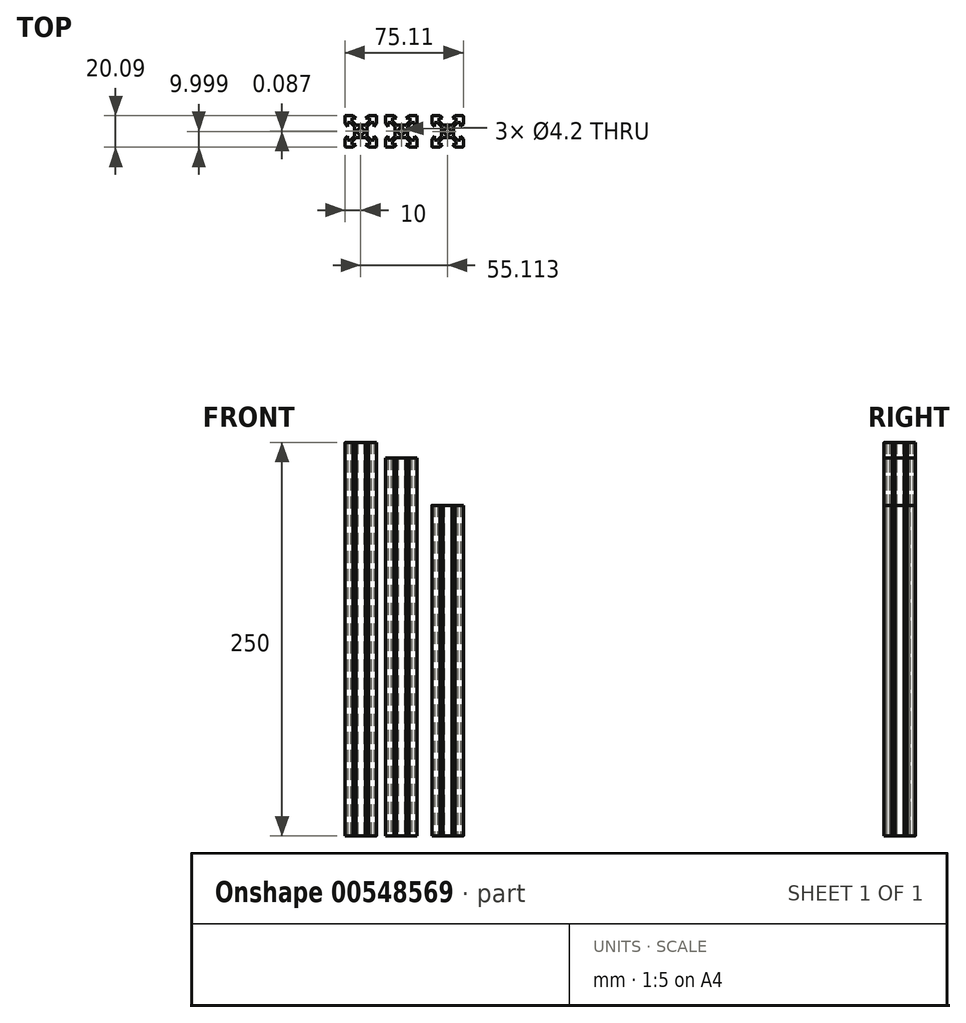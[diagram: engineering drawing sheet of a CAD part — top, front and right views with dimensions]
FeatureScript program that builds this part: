
annotation { "Feature Type Name" : "Feature", "Feature Type Description" : "" }
export const myFeature = defineFeature(function(context is Context, id is Id, definition is map)
    precondition{}
    {
        {
            var Q0;
            Q0=qCreatedBy(makeId("Top.planeOp"),FACE);
            var sketch = newSketch(context, id + "F0", { "sketchPlane" : qUnion([Q0])});
            skPoint(sketch, "E0.middle", {"position": v(0, 0) * mm});
            skLineSegment(sketch, "E1", {"start": v(10, -9.5) * mm, "end": v(10, -4.78) * mm});
            skLineSegment(sketch, "E2", {"start": v(9.5, -10) * mm, "end": v(4.78, -10) * mm});
            skCircle(sketch, "E3", {"center": v(0, 0) * mm, "radius": 2.1 * mm});
            skLineSegment(sketch, "E4", {"start": v(8.32, -3.1) * mm, "end": v(8.32, -5.5) * mm});
            skLineSegment(sketch, "E5", {"start": v(3.1, -8.33) * mm, "end": v(5.5, -8.33) * mm});
            skLineSegment(sketch, "E6", {"start": v(8.32, -3.1) * mm, "end": v(8.32, 0) * mm, "construction": true});
            skLineSegment(sketch, "E7", {"start": v(3.1, -8.33) * mm, "end": v(0, -8.33) * mm, "construction": true});
            skLineSegment(sketch, "E8", {"start": v(5.5, -5.5) * mm, "end": v(5.5, 0) * mm, "construction": true});
            skLineSegment(sketch, "E9", {"start": v(5.5, -5.5) * mm, "end": v(0, -5.5) * mm, "construction": true});
            skLineSegment(sketch, "E10", {"start": v(10, -4.78) * mm, "end": v(10, 0) * mm, "construction": true});
            skLineSegment(sketch, "E11", {"start": v(10, -4.78) * mm, "end": v(8.32, -3.1) * mm});
            skLineSegment(sketch, "E12", {"start": v(4.78, -10) * mm, "end": v(0, -10) * mm, "construction": true});
            skLineSegment(sketch, "E13", {"start": v(4.78, -10) * mm, "end": v(3.1, -8.33) * mm});
            skLineSegment(sketch, "E14", {"start": v(2.98, -3.9) * mm, "end": v(5.5, -6.42) * mm});
            skLineSegment(sketch, "E15", {"start": v(8.32, -5.5) * mm, "end": v(6.42, -5.5) * mm});
            skLineSegment(sketch, "E16", {"start": v(5.5, -8.33) * mm, "end": v(5.5, -6.42) * mm});
            skLineSegment(sketch, "E17.trimOffspring", {"start": v(3.9, -2.98) * mm, "end": v(6.42, -5.5) * mm});
            skLineSegment(sketch, "E18.MirrorCS", {"start": v(8.32, 3.1) * mm, "end": v(8.32, 5.5) * mm});
            skLineSegment(sketch, "E19.MirrorCS", {"start": v(3.1, 8.33) * mm, "end": v(5.5, 8.33) * mm});
            skLineSegment(sketch, "E20.MirrorCS", {"start": v(4.78, 10) * mm, "end": v(3.1, 8.33) * mm});
            skLineSegment(sketch, "E21.MirrorCS", {"start": v(2.98, 3.9) * mm, "end": v(5.5, 6.42) * mm});
            skLineSegment(sketch, "E22.MirrorCS", {"start": v(5.5, 8.33) * mm, "end": v(5.5, 6.42) * mm});
            skLineSegment(sketch, "E23.MirrorCS", {"start": v(10, 9.5) * mm, "end": v(10, 4.78) * mm});
            skLineSegment(sketch, "E24.MirrorCS", {"start": v(8.32, 5.5) * mm, "end": v(6.42, 5.5) * mm});
            skLineSegment(sketch, "E25.MirrorCS", {"start": v(10, 4.78) * mm, "end": v(8.32, 3.1) * mm});
            skLineSegment(sketch, "E26.MirrorCS", {"start": v(9.5, 10) * mm, "end": v(4.78, 10) * mm});
            skLineSegment(sketch, "E27.MirrorCS", {"start": v(3.9, 2.98) * mm, "end": v(6.42, 5.5) * mm});
            skLineSegment(sketch, "E28.MirrorCS", {"start": v(-9.5, 10) * mm, "end": v(-4.78, 10) * mm});
            skLineSegment(sketch, "E29.MirrorCS", {"start": v(-5.5, 8.33) * mm, "end": v(-5.5, 6.42) * mm});
            skLineSegment(sketch, "E30.MirrorCS", {"start": v(-8.32, 5.5) * mm, "end": v(-6.42, 5.5) * mm});
            skLineSegment(sketch, "E31.MirrorCS", {"start": v(-4.78, 10) * mm, "end": v(-3.1, 8.33) * mm});
            skLineSegment(sketch, "E32.MirrorCS", {"start": v(-3.1, 8.33) * mm, "end": v(-5.5, 8.33) * mm});
            skLineSegment(sketch, "E33.MirrorCS", {"start": v(-2.98, 3.9) * mm, "end": v(-5.5, 6.42) * mm});
            skLineSegment(sketch, "E34.MirrorCS", {"start": v(-8.32, 3.1) * mm, "end": v(-8.32, 5.5) * mm});
            skLineSegment(sketch, "E35.MirrorCS", {"start": v(-10, 9.5) * mm, "end": v(-10, 4.78) * mm});
            skLineSegment(sketch, "E36.MirrorCS", {"start": v(-10, 4.78) * mm, "end": v(-8.32, 3.1) * mm});
            skLineSegment(sketch, "E37.MirrorCS", {"start": v(-3.9, 2.98) * mm, "end": v(-6.42, 5.5) * mm});
            skLineSegment(sketch, "E38.MirrorCS", {"start": v(-9.5, -10) * mm, "end": v(-4.78, -10) * mm});
            skLineSegment(sketch, "E39.MirrorCS", {"start": v(-8.32, -5.5) * mm, "end": v(-6.42, -5.5) * mm});
            skLineSegment(sketch, "E40.MirrorCS", {"start": v(-3.1, -8.33) * mm, "end": v(-5.5, -8.33) * mm});
            skLineSegment(sketch, "E41.MirrorCS", {"start": v(-8.32, -3.1) * mm, "end": v(-8.32, -5.5) * mm});
            skLineSegment(sketch, "E42.MirrorCS", {"start": v(-10, -4.78) * mm, "end": v(-8.32, -3.1) * mm});
            skLineSegment(sketch, "E43.MirrorCS", {"start": v(-3.9, -2.98) * mm, "end": v(-6.42, -5.5) * mm});
            skLineSegment(sketch, "E44.MirrorCS", {"start": v(-10, -9.5) * mm, "end": v(-10, -4.78) * mm});
            skLineSegment(sketch, "E45.MirrorCS", {"start": v(-4.78, -10) * mm, "end": v(-3.1, -8.33) * mm});
            skLineSegment(sketch, "E46.MirrorCS", {"start": v(-2.98, -3.9) * mm, "end": v(-5.5, -6.42) * mm});
            skLineSegment(sketch, "E47.MirrorCS", {"start": v(-5.5, -8.33) * mm, "end": v(-5.5, -6.42) * mm});
            skLineSegment(sketch, "E48.bottom", {"start": v(2.98, 3.9) * mm, "end": v(-2.98, 3.9) * mm});
            skLineSegment(sketch, "E48.top", {"start": v(2.98, -3.9) * mm, "end": v(-2.98, -3.9) * mm});
            skLineSegment(sketch, "E48.left", {"start": v(3.9, 2.98) * mm, "end": v(3.9, -2.98) * mm});
            skLineSegment(sketch, "E48.right", {"start": v(-3.9, 2.98) * mm, "end": v(-3.9, -2.98) * mm});
            skPoint(sketch, "E49.orphan", {"position": v(3.9, -3.9) * mm});
            skPoint(sketch, "E50.orphan", {"position": v(3.9, 3.9) * mm});
            skPoint(sketch, "E51.orphan", {"position": v(-3.9, 3.9) * mm});
            skPoint(sketch, "E52.orphan", {"position": v(-3.9, -3.9) * mm});
            skPoint(sketch, "E53.visualSharp", {"position": v(10, -10) * mm});
            skArc(sketch, "E53.filletArc", {"start": v(9.5, -10) * mm, "mid": v(9.85, -9.85) * mm, "end": v(10, -9.5) * mm});
            skPoint(sketch, "E54.visualSharp", {"position": v(10, 10) * mm});
            skArc(sketch, "E54.filletArc", {"start": v(10, 9.5) * mm, "mid": v(9.85, 9.85) * mm, "end": v(9.5, 10) * mm});
            skPoint(sketch, "E55.visualSharp", {"position": v(-10, 10) * mm});
            skArc(sketch, "E55.filletArc", {"start": v(-9.5, 10) * mm, "mid": v(-9.85, 9.85) * mm, "end": v(-10, 9.5) * mm});
            skPoint(sketch, "E56.visualSharp", {"position": v(-10, -10) * mm});
            skArc(sketch, "E56.filletArc", {"start": v(-10, -9.5) * mm, "mid": v(-9.85, -9.85) * mm, "end": v(-9.5, -10) * mm});
            skSolve(sketch);
        }
        {
            var Q0;
            Q0=makeQuery(id+"F0.imprint","IMPRINT",FACE,{"disambiguationData":[TD([[makeQuery(id+"F0.imprint","IMPRINT",EDGE,{"derivedFrom":sQuery(id+"F0.wireOp",EDGE,"E1")}),1.0]])]});
            extrude(context, id + "F1", {"entities" : qUnion([Q0]), "depth" : 250 * mm, "offsetDistance" : 25 * mm});
        }
        {
            var Q0;
            Q0=qCreatedBy(makeId("Top.planeOp"),FACE);
            var sketch = newSketch(context, id + "F2", { "sketchPlane" : qUnion([Q0])});
            skPoint(sketch, "E57.middle", {"position": v(25.78, 0) * mm});
            skLineSegment(sketch, "E58", {"start": v(35.78, -10) * mm, "end": v(35.78, -4.77) * mm});
            skLineSegment(sketch, "E59", {"start": v(35.78, -10) * mm, "end": v(30.56, -10) * mm});
            skCircle(sketch, "E60", {"center": v(25.78, 0) * mm, "radius": 2.1 * mm});
            skLineSegment(sketch, "E61", {"start": v(34.1, -3.1) * mm, "end": v(34.1, -5.5) * mm});
            skLineSegment(sketch, "E62", {"start": v(28.88, -8.32) * mm, "end": v(31.28, -8.32) * mm});
            skLineSegment(sketch, "E63", {"start": v(34.1, -3.1) * mm, "end": v(34.1, 0) * mm, "construction": true});
            skLineSegment(sketch, "E64", {"start": v(28.88, -8.32) * mm, "end": v(25.78, -8.32) * mm, "construction": true});
            skLineSegment(sketch, "E65", {"start": v(31.28, -5.5) * mm, "end": v(31.28, 0) * mm, "construction": true});
            skLineSegment(sketch, "E66", {"start": v(31.28, -5.5) * mm, "end": v(25.78, -5.5) * mm, "construction": true});
            skLineSegment(sketch, "E67", {"start": v(35.78, -4.77) * mm, "end": v(35.78, 0) * mm, "construction": true});
            skLineSegment(sketch, "E68", {"start": v(35.78, -4.77) * mm, "end": v(34.1, -3.1) * mm});
            skLineSegment(sketch, "E69", {"start": v(30.56, -10) * mm, "end": v(25.78, -10) * mm, "construction": true});
            skLineSegment(sketch, "E70", {"start": v(30.56, -10) * mm, "end": v(28.88, -8.32) * mm});
            skLineSegment(sketch, "E71", {"start": v(28.76, -3.9) * mm, "end": v(31.28, -6.41) * mm});
            skLineSegment(sketch, "E72", {"start": v(34.1, -5.5) * mm, "end": v(32.2, -5.5) * mm});
            skLineSegment(sketch, "E73", {"start": v(31.28, -8.32) * mm, "end": v(31.28, -6.41) * mm});
            skLineSegment(sketch, "E74.trimOffspring", {"start": v(29.68, -2.97) * mm, "end": v(32.2, -5.5) * mm});
            skLineSegment(sketch, "E75.MirrorCS", {"start": v(34.1, 3.1) * mm, "end": v(34.1, 5.5) * mm});
            skLineSegment(sketch, "E76.MirrorCS", {"start": v(28.88, 8.33) * mm, "end": v(31.28, 8.33) * mm});
            skLineSegment(sketch, "E77.MirrorCS", {"start": v(30.56, 10) * mm, "end": v(28.88, 8.33) * mm});
            skLineSegment(sketch, "E78.MirrorCS", {"start": v(28.76, 3.9) * mm, "end": v(31.28, 6.43) * mm});
            skLineSegment(sketch, "E79.MirrorCS", {"start": v(31.28, 8.33) * mm, "end": v(31.28, 6.43) * mm});
            skLineSegment(sketch, "E80.MirrorCS", {"start": v(35.78, 10) * mm, "end": v(35.78, 4.78) * mm});
            skLineSegment(sketch, "E81.MirrorCS", {"start": v(34.1, 5.5) * mm, "end": v(32.2, 5.5) * mm});
            skLineSegment(sketch, "E82.MirrorCS", {"start": v(35.78, 4.78) * mm, "end": v(34.1, 3.1) * mm});
            skLineSegment(sketch, "E83.MirrorCS", {"start": v(35.78, 10) * mm, "end": v(30.56, 10) * mm});
            skLineSegment(sketch, "E84.MirrorCS", {"start": v(29.68, 2.99) * mm, "end": v(32.2, 5.5) * mm});
            skLineSegment(sketch, "E85.MirrorCS", {"start": v(15.78, 10) * mm, "end": v(21, 10) * mm});
            skLineSegment(sketch, "E86.MirrorCS", {"start": v(20.28, 8.33) * mm, "end": v(20.28, 6.43) * mm});
            skLineSegment(sketch, "E87.MirrorCS", {"start": v(17.46, 5.5) * mm, "end": v(19.36, 5.5) * mm});
            skLineSegment(sketch, "E88.MirrorCS", {"start": v(21, 10) * mm, "end": v(22.68, 8.33) * mm});
            skLineSegment(sketch, "E89.MirrorCS", {"start": v(22.68, 8.33) * mm, "end": v(20.28, 8.33) * mm});
            skLineSegment(sketch, "E90.MirrorCS", {"start": v(22.8, 3.9) * mm, "end": v(20.28, 6.43) * mm});
            skLineSegment(sketch, "E91.MirrorCS", {"start": v(17.46, 3.1) * mm, "end": v(17.46, 5.5) * mm});
            skLineSegment(sketch, "E92.MirrorCS", {"start": v(15.78, 10) * mm, "end": v(15.78, 4.78) * mm});
            skLineSegment(sketch, "E93.MirrorCS", {"start": v(15.78, 4.78) * mm, "end": v(17.46, 3.1) * mm});
            skLineSegment(sketch, "E94.MirrorCS", {"start": v(21.88, 2.99) * mm, "end": v(19.36, 5.5) * mm});
            skLineSegment(sketch, "E95.MirrorCS", {"start": v(15.78, -10) * mm, "end": v(21, -10) * mm});
            skLineSegment(sketch, "E96.MirrorCS", {"start": v(17.46, -5.5) * mm, "end": v(19.36, -5.5) * mm});
            skLineSegment(sketch, "E97.MirrorCS", {"start": v(22.68, -8.32) * mm, "end": v(20.28, -8.32) * mm});
            skLineSegment(sketch, "E98.MirrorCS", {"start": v(17.46, -3.1) * mm, "end": v(17.46, -5.5) * mm});
            skLineSegment(sketch, "E99.MirrorCS", {"start": v(15.78, -4.77) * mm, "end": v(17.46, -3.1) * mm});
            skLineSegment(sketch, "E100.MirrorCS", {"start": v(21.88, -2.97) * mm, "end": v(19.36, -5.5) * mm});
            skLineSegment(sketch, "E101.MirrorCS", {"start": v(15.78, -10) * mm, "end": v(15.78, -4.77) * mm});
            skLineSegment(sketch, "E102.MirrorCS", {"start": v(21, -10) * mm, "end": v(22.68, -8.32) * mm});
            skLineSegment(sketch, "E103.MirrorCS", {"start": v(22.8, -3.9) * mm, "end": v(20.28, -6.41) * mm});
            skLineSegment(sketch, "E104.MirrorCS", {"start": v(20.28, -8.32) * mm, "end": v(20.28, -6.41) * mm});
            skLineSegment(sketch, "E105.bottom", {"start": v(28.76, 3.9) * mm, "end": v(22.8, 3.9) * mm});
            skLineSegment(sketch, "E105.top", {"start": v(28.76, -3.9) * mm, "end": v(22.8, -3.9) * mm});
            skLineSegment(sketch, "E105.left", {"start": v(29.68, 2.99) * mm, "end": v(29.68, -2.97) * mm});
            skLineSegment(sketch, "E105.right", {"start": v(21.88, 2.99) * mm, "end": v(21.88, -2.97) * mm});
            skPoint(sketch, "E106.orphan", {"position": v(29.68, -3.9) * mm});
            skPoint(sketch, "E107.orphan", {"position": v(29.68, 3.9) * mm});
            skPoint(sketch, "E108.orphan", {"position": v(21.88, 3.9) * mm});
            skPoint(sketch, "E109.orphan", {"position": v(21.88, -3.9) * mm});
            skSolve(sketch);
        }
        {
            var Q0;
            Q0 = qSketchRegion(id + "F2", true);
            extrude(context, id + "F3", {"entities" : qUnion([Q0]), "depth" : 240 * mm, "offsetDistance" : 25 * mm});
        }
        {
            var Q0;
            Q0=qCreatedBy(makeId("Top.planeOp"),FACE);
            var sketch = newSketch(context, id + "F4", { "sketchPlane" : qUnion([Q0])});
            skPoint(sketch, "E110.middle", {"position": v(55.11, -0.08) * mm});
            skLineSegment(sketch, "E111", {"start": v(65.11, -9.58) * mm, "end": v(65.11, -4.86) * mm});
            skLineSegment(sketch, "E112", {"start": v(64.61, -10.08) * mm, "end": v(59.89, -10.08) * mm});
            skCircle(sketch, "E113", {"center": v(55.11, -0.08) * mm, "radius": 2.1 * mm});
            skLineSegment(sketch, "E114", {"start": v(63.44, -3.18) * mm, "end": v(63.44, -5.58) * mm});
            skLineSegment(sketch, "E115", {"start": v(58.21, -8.4) * mm, "end": v(60.61, -8.4) * mm});
            skLineSegment(sketch, "E116", {"start": v(63.44, -3.18) * mm, "end": v(63.44, -0.08) * mm, "construction": true});
            skLineSegment(sketch, "E117", {"start": v(58.21, -8.4) * mm, "end": v(55.11, -8.4) * mm, "construction": true});
            skLineSegment(sketch, "E118", {"start": v(60.61, -5.58) * mm, "end": v(60.61, -0.08) * mm, "construction": true});
            skLineSegment(sketch, "E119", {"start": v(60.61, -5.58) * mm, "end": v(55.11, -5.58) * mm, "construction": true});
            skLineSegment(sketch, "E120", {"start": v(65.11, -4.86) * mm, "end": v(65.11, -0.08) * mm, "construction": true});
            skLineSegment(sketch, "E121", {"start": v(65.11, -4.86) * mm, "end": v(63.44, -3.18) * mm});
            skLineSegment(sketch, "E122", {"start": v(59.89, -10.08) * mm, "end": v(55.11, -10.08) * mm, "construction": true});
            skLineSegment(sketch, "E123", {"start": v(59.89, -10.08) * mm, "end": v(58.21, -8.4) * mm});
            skLineSegment(sketch, "E124", {"start": v(58.1, -3.98) * mm, "end": v(60.61, -6.5) * mm});
            skLineSegment(sketch, "E125", {"start": v(63.44, -5.58) * mm, "end": v(61.53, -5.58) * mm});
            skLineSegment(sketch, "E126", {"start": v(60.61, -8.4) * mm, "end": v(60.61, -6.5) * mm});
            skLineSegment(sketch, "E127.trimOffspring", {"start": v(59.01, -3.06) * mm, "end": v(61.53, -5.58) * mm});
            skLineSegment(sketch, "E128.MirrorCS", {"start": v(63.44, 3.02) * mm, "end": v(63.44, 5.42) * mm});
            skLineSegment(sketch, "E129.MirrorCS", {"start": v(58.21, 8.24) * mm, "end": v(60.61, 8.24) * mm});
            skLineSegment(sketch, "E130.MirrorCS", {"start": v(59.89, 9.92) * mm, "end": v(58.21, 8.24) * mm});
            skLineSegment(sketch, "E131.MirrorCS", {"start": v(58.1, 3.82) * mm, "end": v(60.61, 6.34) * mm});
            skLineSegment(sketch, "E132.MirrorCS", {"start": v(60.61, 8.24) * mm, "end": v(60.61, 6.34) * mm});
            skLineSegment(sketch, "E133.MirrorCS", {"start": v(65.11, 9.42) * mm, "end": v(65.11, 4.7) * mm});
            skLineSegment(sketch, "E134.MirrorCS", {"start": v(63.44, 5.42) * mm, "end": v(61.53, 5.42) * mm});
            skLineSegment(sketch, "E135.MirrorCS", {"start": v(65.11, 4.7) * mm, "end": v(63.44, 3.02) * mm});
            skLineSegment(sketch, "E136.MirrorCS", {"start": v(64.61, 9.92) * mm, "end": v(59.89, 9.92) * mm});
            skLineSegment(sketch, "E137.MirrorCS", {"start": v(59.01, 2.9) * mm, "end": v(61.53, 5.42) * mm});
            skLineSegment(sketch, "E138.MirrorCS", {"start": v(45.61, 9.92) * mm, "end": v(50.34, 9.92) * mm});
            skLineSegment(sketch, "E139.MirrorCS", {"start": v(49.61, 8.24) * mm, "end": v(49.61, 6.34) * mm});
            skLineSegment(sketch, "E140.MirrorCS", {"start": v(46.79, 5.42) * mm, "end": v(48.7, 5.42) * mm});
            skLineSegment(sketch, "E141.MirrorCS", {"start": v(50.34, 9.92) * mm, "end": v(52.01, 8.24) * mm});
            skLineSegment(sketch, "E142.MirrorCS", {"start": v(52.01, 8.24) * mm, "end": v(49.61, 8.24) * mm});
            skLineSegment(sketch, "E143.MirrorCS", {"start": v(52.13, 3.82) * mm, "end": v(49.61, 6.34) * mm});
            skLineSegment(sketch, "E144.MirrorCS", {"start": v(46.79, 3.02) * mm, "end": v(46.79, 5.42) * mm});
            skLineSegment(sketch, "E145.MirrorCS", {"start": v(45.11, 9.42) * mm, "end": v(45.11, 4.7) * mm});
            skLineSegment(sketch, "E146.MirrorCS", {"start": v(45.11, 4.7) * mm, "end": v(46.79, 3.02) * mm});
            skLineSegment(sketch, "E147.MirrorCS", {"start": v(51.21, 2.9) * mm, "end": v(48.7, 5.42) * mm});
            skLineSegment(sketch, "E148.MirrorCS", {"start": v(45.61, -10.08) * mm, "end": v(50.34, -10.08) * mm});
            skLineSegment(sketch, "E149.MirrorCS", {"start": v(46.79, -5.58) * mm, "end": v(48.7, -5.58) * mm});
            skLineSegment(sketch, "E150.MirrorCS", {"start": v(52.01, -8.4) * mm, "end": v(49.61, -8.4) * mm});
            skLineSegment(sketch, "E151.MirrorCS", {"start": v(46.79, -3.18) * mm, "end": v(46.79, -5.58) * mm});
            skLineSegment(sketch, "E152.MirrorCS", {"start": v(45.11, -4.86) * mm, "end": v(46.79, -3.18) * mm});
            skLineSegment(sketch, "E153.MirrorCS", {"start": v(51.21, -3.06) * mm, "end": v(48.7, -5.58) * mm});
            skLineSegment(sketch, "E154.MirrorCS", {"start": v(45.11, -9.58) * mm, "end": v(45.11, -4.86) * mm});
            skLineSegment(sketch, "E155.MirrorCS", {"start": v(50.34, -10.08) * mm, "end": v(52.01, -8.4) * mm});
            skLineSegment(sketch, "E156.MirrorCS", {"start": v(52.13, -3.98) * mm, "end": v(49.61, -6.5) * mm});
            skLineSegment(sketch, "E157.MirrorCS", {"start": v(49.61, -8.4) * mm, "end": v(49.61, -6.5) * mm});
            skLineSegment(sketch, "E158.bottom", {"start": v(58.1, 3.82) * mm, "end": v(52.13, 3.82) * mm});
            skLineSegment(sketch, "E158.top", {"start": v(58.1, -3.98) * mm, "end": v(52.13, -3.98) * mm});
            skLineSegment(sketch, "E158.left", {"start": v(59.01, 2.9) * mm, "end": v(59.01, -3.06) * mm});
            skLineSegment(sketch, "E158.right", {"start": v(51.21, 2.9) * mm, "end": v(51.21, -3.06) * mm});
            skPoint(sketch, "E159.orphan", {"position": v(59.01, -3.98) * mm});
            skPoint(sketch, "E160.orphan", {"position": v(59.01, 3.82) * mm});
            skPoint(sketch, "E161.orphan", {"position": v(51.21, 3.82) * mm});
            skPoint(sketch, "E162.orphan", {"position": v(51.21, -3.98) * mm});
            skPoint(sketch, "E163.visualSharp", {"position": v(65.11, -10.08) * mm});
            skArc(sketch, "E163.filletArc", {"start": v(64.61, -10.08) * mm, "mid": v(64.97, -9.93) * mm, "end": v(65.11, -9.58) * mm});
            skPoint(sketch, "E164.visualSharp", {"position": v(65.11, 9.92) * mm});
            skArc(sketch, "E164.filletArc", {"start": v(65.11, 9.42) * mm, "mid": v(64.97, 9.77) * mm, "end": v(64.61, 9.92) * mm});
            skPoint(sketch, "E165.visualSharp", {"position": v(45.11, 9.92) * mm});
            skArc(sketch, "E165.filletArc", {"start": v(45.61, 9.92) * mm, "mid": v(45.26, 9.77) * mm, "end": v(45.11, 9.42) * mm});
            skPoint(sketch, "E166.visualSharp", {"position": v(45.11, -10.08) * mm});
            skArc(sketch, "E166.filletArc", {"start": v(45.11, -9.58) * mm, "mid": v(45.26, -9.93) * mm, "end": v(45.61, -10.08) * mm});
            skSolve(sketch);
        }
        {
            var Q0;
            Q0 = qSketchRegion(id + "F4", true);
            extrude(context, id + "F5", {"entities" : qUnion([Q0]), "depth" : 210 * mm, "offsetDistance" : 25 * mm});
        }
    });
